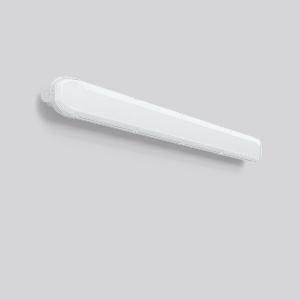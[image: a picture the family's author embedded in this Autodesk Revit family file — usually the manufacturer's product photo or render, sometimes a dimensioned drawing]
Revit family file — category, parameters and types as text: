
# Revit family: planox_451235_009_19_bb73
name_source: partatom
category: Lighting Fixtures
units: mm (PartAtom-declared; Revit-internal decimal feet)

## family parameters
Cut with Voids When Loaded = No
Host = Face
Light Source = No
Part Type = Normal
Room Calculation Point = No
Round Connector Dimension = Use Diameter
Shared = No

## types (1)
- MultiLumen 1 (1 x LED Modul 840, 7200 lm, 4000)
    Apparent Load = 45 VA
    Approval mark = CE
    CIE Flux Codes = 43 73 91 93 100
    Color Rendering = 80
    Color Temperature = 4000
    Default Elevation = 1800 mm
    Description = Series: PLANOX
Classic moisture-proof diffuser luminaire with two-part luminaire design. Housing made of shockproof, UV-resistant plastic (polycarbonate). Injected silicone-based seal with increased resistance even under extreme conditions. Diffuser made of UV-resistant opal plastic (PMMA) with excellent light transmission of up to 90% Diffuser fixed by stainless steel clips for easy installation and opening. Symmetrical light distribution. Homogeneous light distribution. Flexible and easy installation thanks to sliding quick-fix brackets made of stainless steel and diffuser with integrated gear tray as well as variable cable entry (face or rear sided). Suitable for Ceiling mounting, Suspension cable/chain, Wall (surface). Ceiling mounting stainless steel brackets and triangular brackets for pendant mounting included in delivery. MultiLumen: 2 steps adjustable luminous flux. Factory setting is HO (high lumen). Through-wiring (2.5mm2) as standard. With integrated HF movement sensor. Movement sensor functional parameters: Holding time: 5 sec. - 10 or 15 min., adjustable in 4 steps. Range: up to 8 m, adjustable in up to 4 steps. Brightness sensor: adjustable in up to 4 steps. Factory setting: hold time 5 sec., brightness threshold deactivated, detection range 100%. Luminaire with limited surface temperature in accordance with EN 60598-2-24 for use in environments in which a deposit of conductive dust on the luminaire can be expected. Suitable for lighting in public car parks and public off-street parking spaces according to DIN 67528. Environmentally friendly and resource-saving due to replaceable components. 
Colour: light grey (RAL 7035)
Length: 1454 mm
Width: 102 mm
Height: 85 mm
Lamp: LED
Socket: without socket
Colour temperature: 4000K
Colour rendering index (CRI): 80
System power: 45 W
Rated luminous flux: 7200 lm
Beam angle Down: 130° / 104°
Luminous efficiency: 160 lm/W
System power 2: 58 W
Rated luminous flux 2: 9200 lm
Luminous efficiency 2: 159 lm/W
Control gear: Regulated power supply
Protection class: I
Type of protection: IP 66
    Height = 85 mm
    Lamp = 1 x LED Modul 840
    Lamp Light Flux = 7200 lm
    Lamp count = 1
    Length = 1454 mm
    Lifetime = 50000 h
    Luminous efficacy = 160 lm/W
    Manufacturer = RZB
    ModVariant = No
    Model = 451235.009.19
    Mounting Place = Ceiling, Wall
    Mounting Type = Surface mounted
    Number of Poles = 1
    OnlyDefault = Yes
    Power Factor = 1
    Product Name = PLANOX
    Product group = Surface mounted luminaires for moist/humid enviroments
    ProductGroupID = 308
    Protection Class = Protection class I
    Protection Degree = IP 66
    RLX_Detail_Level = 1
    RLX_Emergency_Light_Flux = 0 lm
    RLX_Emergency_Type = 0
    RLX_Emergency_Type_DB = No
    RlxData = <blob elided: 54761 chars, md5=bc4e2a64>
    Socket = socket
    Standby Power = 0 W
    System Light Flux = 7200 lm
    System Power = 45 W
    Type Comments = MultiLumen 1
    Type Image = 451232.009.jpg
    URL = http://relux.com
    VarID = multilumen_1
    Voltage = 230 V
    Voltage Range = 220-240 V
    Weight = 0.00 kg
    Width = 102 mm

## geometry (parser evidence)
native form markers: Blend x4, Sweep x16
no freeform markers — native parametric forms only
